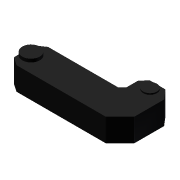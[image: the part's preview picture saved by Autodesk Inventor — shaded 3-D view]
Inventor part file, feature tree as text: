
AUTODESK INVENTOR PART (.ipt)
format: ipt  version: 2012 (Build 160160000, 160)  size: 112,640 bytes
history: native  units: mm
features: extrude x3, sketch x1
ambient origin geometry x8: Origin, YZ Plane, XZ Plane, XY Plane, X Axis, Y Axis, Z Axis, Center Point
bodies: Solid1 (feature_tree)
feature tree (4):
  sketch  "Sketch1"  dims[d0=36.75mm d1=0.0mm d2=47.0mm d3=0.0mm d4=41.0mm d5=0.0mm]
  extrude  "Extrusion1"  Depth=47.0mm TaperAngle=0.0deg
  extrude  "Extrusion2"  Depth=41.0mm TaperAngle=0.0deg
  extrude  "Extrusion3"  [1 undecoded]
note: 1 required parameter value undecoded (feature->parameter linkage not recoverable at this tier; creation-order binding heuristic only, values carry confidence <= 0.55)
